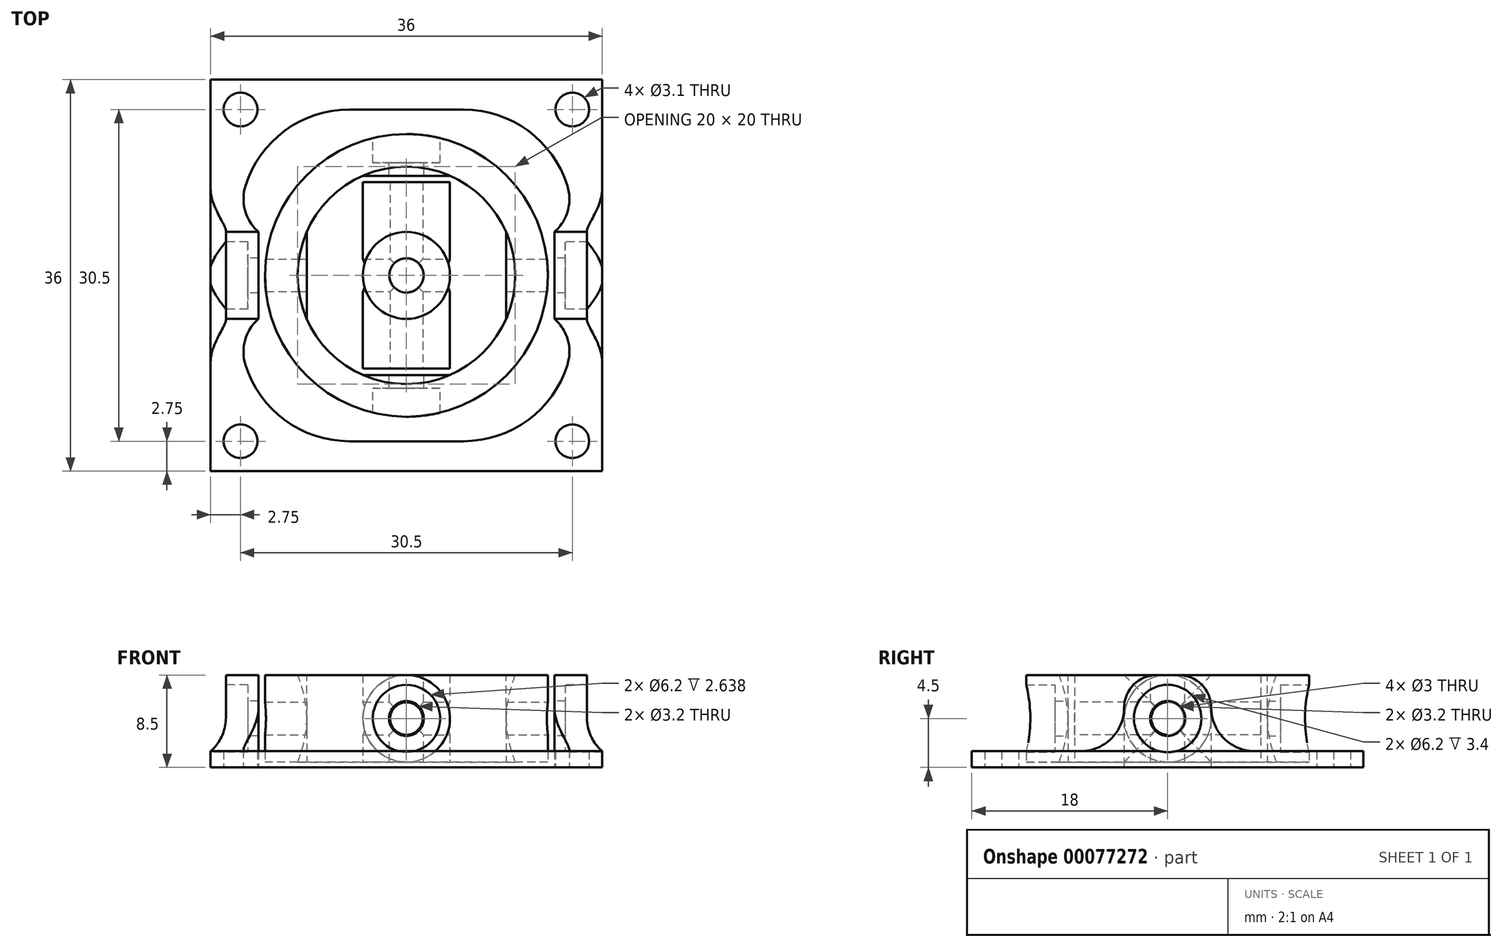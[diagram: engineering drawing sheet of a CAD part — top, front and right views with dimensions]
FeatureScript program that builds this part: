
annotation { "Feature Type Name" : "Feature", "Feature Type Description" : "" }
export const myFeature = defineFeature(function(context is Context, id is Id, definition is map)
    precondition{}
    {
        {
            var Q0;
            Q0=qCreatedBy(makeId("Top.planeOp"),FACE);
            var sketch = newSketch(context, id + "F0", { "sketchPlane" : qUnion([Q0])});
            skLineSegment(sketch, "E0.bottom", {"start": v(18, 18) * mm, "end": v(-18, 18) * mm});
            skLineSegment(sketch, "E0.top", {"start": v(18, -18) * mm, "end": v(-18, -18) * mm});
            skLineSegment(sketch, "E0.left", {"start": v(18, 18) * mm, "end": v(18, -18) * mm});
            skLineSegment(sketch, "E0.right", {"start": v(-18, 18) * mm, "end": v(-18, -18) * mm});
            skPoint(sketch, "E0.middle", {"position": v(0, 0) * mm});
            skLineSegment(sketch, "E1.bottom", {"start": v(15.25, 15.25) * mm, "end": v(-15.25, 15.25) * mm, "construction": true});
            skLineSegment(sketch, "E1.top", {"start": v(15.25, -15.25) * mm, "end": v(-15.25, -15.25) * mm, "construction": true});
            skLineSegment(sketch, "E1.left", {"start": v(15.25, 15.25) * mm, "end": v(15.25, -15.25) * mm, "construction": true});
            skLineSegment(sketch, "E1.right", {"start": v(-15.25, 15.25) * mm, "end": v(-15.25, -15.25) * mm, "construction": true});
            skCircle(sketch, "E2", {"center": v(-15.25, 15.25) * mm, "radius": 1.55 * mm, "construction": true});
            skCircle(sketch, "E3", {"center": v(15.25, 15.25) * mm, "radius": 1.55 * mm, "construction": true});
            skCircle(sketch, "E4", {"center": v(15.25, -15.25) * mm, "radius": 1.55 * mm, "construction": true});
            skCircle(sketch, "E5", {"center": v(-15.25, -15.25) * mm, "radius": 1.55 * mm, "construction": true});
            skSolve(sketch);
        }
        {
            var Q0;
            Q0=qCreatedBy(makeId("Top.planeOp"),FACE);
            var sketch = newSketch(context, id + "F1", { "sketchPlane" : qUnion([Q0])});
            skCircle(sketch, "E6", {"center": v(0, 0) * mm, "radius": 13 * mm});
            skCircle(sketch, "E7", {"center": v(0, 0) * mm, "radius": 10 * mm});
            skLineSegment(sketch, "E8", {"start": v(10, 0) * mm, "end": v(13, 0) * mm, "construction": true});
            skCircle(sketch, "E9", {"center": v(0, 0) * mm, "radius": 1.57 * mm, "construction": true});
            skCircle(sketch, "E10", {"center": v(0, 0) * mm, "radius": 4 * mm});
            skLineSegment(sketch, "E11", {"start": v(0, 4) * mm, "end": v(0, -4) * mm, "construction": true});
            skLineSegment(sketch, "E12", {"start": v(0, 0) * mm, "end": v(10, 0) * mm, "construction": true});
            skSolve(sketch);
        }
        {
            var Q0;
            Q0=qCreatedBy(makeId("Top.planeOp"),FACE);
            var sketch = newSketch(context, id + "F20", { "sketchPlane" : qUnion([Q0])});
            skCircle(sketch, "E13.0", {"center": v(0, 0) * mm, "radius": 10 * mm, "construction": true});
            skLineSegment(sketch, "E14", {"start": v(0, 9.17) * mm, "end": v(-4, 9.17) * mm});
            skLineSegment(sketch, "E15", {"start": v(0, 0) * mm, "end": v(0, -10) * mm, "construction": true});
            skLineSegment(sketch, "E16", {"start": v(-4, 9.17) * mm, "end": v(-4, 12.17) * mm});
            skLineSegment(sketch, "E17", {"start": v(-4, 12.17) * mm, "end": v(0, 12.17) * mm});
            skLineSegment(sketch, "E18", {"start": v(0, 12.17) * mm, "end": v(0, 9.17) * mm});
            skLineSegment(sketch, "E19", {"start": v(0, 0) * mm, "end": v(10, 0) * mm, "construction": true});
            skLineSegment(sketch, "E20.MirrorCS", {"start": v(-4, -12.17) * mm, "end": v(0, -12.17) * mm});
            skLineSegment(sketch, "E21.MirrorCS", {"start": v(-4, -9.17) * mm, "end": v(-4, -12.17) * mm});
            skLineSegment(sketch, "E22.MirrorCS", {"start": v(0, -12.17) * mm, "end": v(0, -9.17) * mm});
            skLineSegment(sketch, "E23.MirrorCS", {"start": v(0, -9.17) * mm, "end": v(-4, -9.17) * mm});
            skLineSegment(sketch, "E24", {"start": v(-4, 8.57) * mm, "end": v(-4, -8.57) * mm});
            skLineSegment(sketch, "E25", {"start": v(-4, 8.57) * mm, "end": v(0, 8.57) * mm});
            skLineSegment(sketch, "E26", {"start": v(-4, -8.57) * mm, "end": v(0, -8.57) * mm});
            skLineSegment(sketch, "E27", {"start": v(0, 8.57) * mm, "end": v(0, -8.57) * mm});
            skSolve(sketch);
        }
        {
            var Q0;
            Q0=qCreatedBy(makeId("Top.planeOp"),FACE);
            var sketch = newSketch(context, id + "F2", { "sketchPlane" : qUnion([Q0])});
            skLineSegment(sketch, "E28.0", {"start": v(0, -9.17) * mm, "end": v(-4, -9.17) * mm, "construction": true});
            skLineSegment(sketch, "E29.0", {"start": v(0, 9.17) * mm, "end": v(-4, 9.17) * mm, "construction": true});
            skLineSegment(sketch, "E30", {"start": v(0, 9.17) * mm, "end": v(0, 10.37) * mm, "construction": true});
            skLineSegment(sketch, "E31", {"start": v(0, 0) * mm, "end": v(0, 9.17) * mm, "construction": true});
            skLineSegment(sketch, "E32.bottom", {"start": v(0, 10.37) * mm, "end": v(-3.1, 10.37) * mm});
            skLineSegment(sketch, "E32.top", {"start": v(0, 16.03) * mm, "end": v(-3.1, 16.03) * mm});
            skLineSegment(sketch, "E32.left", {"start": v(0, 10.37) * mm, "end": v(0, 16.03) * mm});
            skLineSegment(sketch, "E32.right", {"start": v(-3.1, 10.37) * mm, "end": v(-3.1, 16.03) * mm});
            skLineSegment(sketch, "E33.bottom", {"start": v(0, 9.17) * mm, "end": v(-1.6, 9.17) * mm});
            skLineSegment(sketch, "E33.top", {"start": v(0, 10.37) * mm, "end": v(-1.6, 10.37) * mm});
            skLineSegment(sketch, "E33.left", {"start": v(0, 9.17) * mm, "end": v(0, 10.37) * mm});
            skLineSegment(sketch, "E33.right", {"start": v(-1.6, 9.17) * mm, "end": v(-1.6, 10.37) * mm});
            skLineSegment(sketch, "E34", {"start": v(0, 0) * mm, "end": v(12.38, 0) * mm, "construction": true});
            skLineSegment(sketch, "E35.MirrorCS", {"start": v(-3.1, -10.37) * mm, "end": v(-3.1, -16.03) * mm});
            skLineSegment(sketch, "E36.MirrorCS", {"start": v(0, -10.37) * mm, "end": v(0, -16.03) * mm});
            skLineSegment(sketch, "E37.MirrorCS", {"start": v(0, -10.37) * mm, "end": v(-3.1, -10.37) * mm});
            skLineSegment(sketch, "E38.MirrorCS", {"start": v(0, -9.17) * mm, "end": v(0, -10.37) * mm, "construction": true});
            skLineSegment(sketch, "E39.MirrorCS", {"start": v(0, -16.03) * mm, "end": v(-3.1, -16.03) * mm});
            skLineSegment(sketch, "E40.MirrorCS", {"start": v(-1.6, -9.17) * mm, "end": v(-1.6, -10.37) * mm});
            skLineSegment(sketch, "E41", {"start": v(-1.6, -9.17) * mm, "end": v(0, -9.17) * mm});
            skLineSegment(sketch, "E42", {"start": v(0, -10.37) * mm, "end": v(0, -9.17) * mm});
            skSolve(sketch);
        }
        {
            var Q0;
            Q0=makeQuery(id+"F1.imprint","IMPRINT",FACE,{"disambiguationData":[TD([[makeQuery(id+"F1.imprint","IMPRINT",EDGE,{"derivedFrom":sQuery(id+"F1.wireOp",EDGE,"E10")}),1.0]])]});
            extrude(context, id + "F3", {"entities" : qUnion([Q0]), "endBound" : BoundingType.SYMMETRIC, "depth" : 8 * mm});
        }
        {
            var Q0;
            Q0=makeQuery(id+"F1.imprint","IMPRINT",FACE,{"disambiguationData":[TD([[makeQuery(id+"F1.imprint","IMPRINT",EDGE,{"derivedFrom":sQuery(id+"F1.wireOp",EDGE,"E6")}),1.0]])]});
            extrude(context, id + "F4", {"entities" : qUnion([Q0]), "endBound" : BoundingType.SYMMETRIC, "depth" : 8 * mm});
        }
        {
            var Q0;
            Q0=makeQuery(id+"F20.imprint","IMPRINT",FACE,{"disambiguationData":[TD([[makeQuery(id+"F20.imprint","IMPRINT",EDGE,{"derivedFrom":sQuery(id+"F20.wireOp",EDGE,"E14")}),-1.0]])]});
            var Q1;
            Q1=sQuery(id+"F20.wireOp",EDGE,"E15");
            revolve(context, id + "F5", {"entities" : qUnion([Q0]), "axis" : qUnion([Q1]), "revolveType" : RevolveType.FULL});
        }
        {
            var Q0;
            Q0=makeQuery(id+"F20.imprint","IMPRINT",FACE,{"disambiguationData":[TD([[makeQuery(id+"F20.imprint","IMPRINT",EDGE,{"derivedFrom":sQuery(id+"F20.wireOp",EDGE,"E24")}),1.0]])]});
            var Q1;
            Q1=sQuery(id+"F20.wireOp",EDGE,"E27");
            revolve(context, id + "F21", {"operationType" : NewBodyOperationType.ADD, "entities" : qUnion([Q0]), "axis" : qUnion([Q1]), "revolveType" : RevolveType.FULL});
        }
        {
            var Q0;
            Q0=qCreatedBy(makeId("Front.planeOp"),FACE);
            var sketch = newSketch(context, id + "F22", { "sketchPlane" : qUnion([Q0])});
            skLineSegment(sketch, "E43", {"start": v(0, 0) * mm, "end": v(0, 28.15) * mm, "construction": true});
            skSolve(sketch);
        }
        {
            var Q0;
            Q0=makeQuery(id+"F5.opRevolve","SWEPT_BODY",BODY,{"disambiguationData":[OSD([sQuery(id+"F20.wireOp",EDGE,"E14"),sQuery(id+"F20.wireOp",EDGE,"E16"),sQuery(id+"F20.wireOp",EDGE,"E17"),sQuery(id+"F20.wireOp",EDGE,"E18")])]});
            var Q1;
            Q1=sQuery(id+"F22.wireOp",EDGE,"E43");
            circularPattern(context, id + "F6", {"operationType" : NewBodyOperationType.ADD, "entities" : qUnion([Q0]), "axis" : qUnion([Q1]), "angle" : 90 * degree, "instanceCount" : 4});
        }
        {
            var Q0;
            Q0=makeQuery(id+"F2.imprint","IMPRINT",FACE,{"disambiguationData":[TD([[makeQuery(id+"F2.imprint","IMPRINT",EDGE,{"derivedFrom":sQuery(id+"F2.wireOp",EDGE,"E32.bottom")}),-1.0]])]});
            var Q1;
            {var subQ1=sQuery(id+"F2.wireOp",EDGE,"E35.MirrorCS");Q1=makeQuery(id+"F2.imprint","IMPRINT",FACE,{"disambiguationData":[TD([[makeQuery(id+"F2.imprint","IMPRINT",EDGE,{"derivedFrom":subQ1}),1.0]])]});}
            var Q2;
            {var subQ2=sQuery(id+"F2.wireOp",EDGE,"E40.MirrorCS");Q2=makeQuery(id+"F2.imprint","IMPRINT",FACE,{"disambiguationData":[TD([[makeQuery(id+"F2.imprint","IMPRINT",EDGE,{"derivedFrom":subQ2}),1.0]])]});}
            var Q3;
            Q3=makeQuery(id+"F2.imprint","IMPRINT",FACE,{"disambiguationData":[TD([[makeQuery(id+"F2.imprint","IMPRINT",EDGE,{"derivedFrom":sQuery(id+"F2.wireOp",EDGE,"E33.bottom")}),-1.0]])]});
            var Q4;
            Q4=sQuery(id+"F2.wireOp",EDGE,"E31");
            revolve(context, id + "F23", {"operationType" : NewBodyOperationType.REMOVE, "entities" : qUnion([Q0, Q1, Q2, Q3]), "axis" : qUnion([Q4]), "revolveType" : RevolveType.FULL, "oppositeDirection" : true});
        }
        {
            var Q0;
            Q0=qCreatedBy(makeId("Top.planeOp"),FACE);
            var sketch = newSketch(context, id + "F24", { "sketchPlane" : qUnion([Q0])});
            skCircle(sketch, "E44.0", {"center": v(0, 0) * mm, "radius": 1.57 * mm});
            skSolve(sketch);
        }
        {
            var Q0;
            Q0=makeQuery(id+"F24.imprint","IMPRINT",FACE,{"disambiguationData":[TD([[makeQuery(id+"F24.imprint","IMPRINT",EDGE,{"derivedFrom":sQuery(id+"F24.wireOp",EDGE,"E44.0")}),1.0]])]});
            extrude(context, id + "F7", {"entities" : qUnion([Q0]), "operationType" : NewBodyOperationType.REMOVE, "endBound" : BoundingType.THROUGH_ALL, "oppositeDirection" : true, "depth" : 25 * mm, "hasSecondDirection" : true, "secondDirectionBound" : SecondDirectionBoundingType.THROUGH_ALL, "secondDirectionOppositeDirection" : false, "secondDirectionDepth" : 25 * mm});
        }
        {
            var Q0;
            Q0=qCreatedBy(makeId("Front.planeOp"),FACE);
            var sketch = newSketch(context, id + "F8", { "sketchPlane" : qUnion([Q0])});
            skCircle(sketch, "E45", {"center": v(0, 0) * mm, "radius": 1.5 * mm});
            skSolve(sketch);
        }
        {
            var Q0;
            Q0=makeQuery(id+"F8.imprint","IMPRINT",FACE,{"disambiguationData":[TD([[makeQuery(id+"F8.imprint","IMPRINT",EDGE,{"derivedFrom":sQuery(id+"F8.wireOp",EDGE,"E45")}),1.0]])]});
            extrude(context, id + "F25", {"entities" : qUnion([Q0]), "operationType" : NewBodyOperationType.REMOVE, "endBound" : BoundingType.THROUGH_ALL, "oppositeDirection" : true, "depth" : 25 * mm, "hasSecondDirection" : true, "secondDirectionOppositeDirection" : false, "secondDirectionDepth" : 25 * mm});
        }
        {
            var Q0;
            Q0=qCreatedBy(makeId("Right.planeOp"),FACE);
            var sketch = newSketch(context, id + "F9", { "sketchPlane" : qUnion([Q0])});
            skCircle(sketch, "E46", {"center": v(0, 0) * mm, "radius": 1.5 * mm});
            skSolve(sketch);
        }
        {
            var Q0;
            Q0=makeQuery(id+"F9.imprint","IMPRINT",FACE,{"disambiguationData":[TD([[makeQuery(id+"F9.imprint","IMPRINT",EDGE,{"derivedFrom":sQuery(id+"F9.wireOp",EDGE,"E46")}),1.0]])]});
            extrude(context, id + "F26", {"entities" : qUnion([Q0]), "operationType" : NewBodyOperationType.REMOVE, "endBound" : BoundingType.THROUGH_ALL, "oppositeDirection" : true, "depth" : 25 * mm, "hasSecondDirection" : true, "secondDirectionBound" : SecondDirectionBoundingType.THROUGH_ALL, "secondDirectionOppositeDirection" : false, "secondDirectionDepth" : 25 * mm});
        }
        {
            var Q0;
            Q0=qCreatedBy(makeId("Top.planeOp"),FACE);
            var sketch = newSketch(context, id + "F10", { "sketchPlane" : qUnion([Q0])});
            skLineSegment(sketch, "E47.0", {"start": v(-18, 18) * mm, "end": v(-18, -18) * mm});
            skLineSegment(sketch, "E48.0", {"start": v(18, 18) * mm, "end": v(-18, 18) * mm});
            skLineSegment(sketch, "E49.0", {"start": v(18, 18) * mm, "end": v(18, -18) * mm});
            skLineSegment(sketch, "E50.0", {"start": v(18, -18) * mm, "end": v(-18, -18) * mm});
            skCircle(sketch, "E51.0", {"center": v(-15.25, 15.25) * mm, "radius": 1.55 * mm});
            skCircle(sketch, "E52.0", {"center": v(15.25, 15.25) * mm, "radius": 1.55 * mm});
            skCircle(sketch, "E53.0", {"center": v(-15.25, -15.25) * mm, "radius": 1.55 * mm});
            skCircle(sketch, "E54.0", {"center": v(15.25, -15.25) * mm, "radius": 1.55 * mm});
            skLineSegment(sketch, "E55", {"start": v(-5.25, 15.25) * mm, "end": v(5.25, 15.25) * mm});
            skLineSegment(sketch, "E56", {"start": v(15.25, -5.25) * mm, "end": v(15.25, -4) * mm});
            skLineSegment(sketch, "E57", {"start": v(-5.25, -15.25) * mm, "end": v(5.25, -15.25) * mm});
            skLineSegment(sketch, "E58", {"start": v(-15.25, 5.25) * mm, "end": v(-15.25, 4) * mm});
            skArc(sketch, "E59.filletArc", {"start": v(-5.25, 15.25) * mm, "mid": v(-12.32, 12.32) * mm, "end": v(-15.25, 5.25) * mm});
            skArc(sketch, "E60.filletArc", {"start": v(15.25, 5.25) * mm, "mid": v(12.32, 12.32) * mm, "end": v(5.25, 15.25) * mm});
            skArc(sketch, "E61.filletArc", {"start": v(-15.25, -5.25) * mm, "mid": v(-12.32, -12.32) * mm, "end": v(-5.25, -15.25) * mm});
            skArc(sketch, "E62.filletArc", {"start": v(5.25, -15.25) * mm, "mid": v(12.32, -12.32) * mm, "end": v(15.25, -5.25) * mm});
            skCircle(sketch, "E63.0", {"center": v(0, 0) * mm, "radius": 13 * mm, "construction": true});
            skLineSegment(sketch, "E64", {"start": v(-13, 0) * mm, "end": v(-13.6, 0) * mm, "construction": true});
            skLineSegment(sketch, "E65", {"start": v(-13.6, 4) * mm, "end": v(-13.6, -4) * mm});
            skLineSegment(sketch, "E66", {"start": v(-13.6, 4) * mm, "end": v(-15.25, 4) * mm});
            skLineSegment(sketch, "E67", {"start": v(-13.6, -4) * mm, "end": v(-15.25, -4) * mm});
            skLineSegment(sketch, "E68.MirrorCS", {"start": v(13.6, 4) * mm, "end": v(15.25, 4) * mm});
            skLineSegment(sketch, "E69.MirrorCS", {"start": v(13.6, 4) * mm, "end": v(13.6, -4) * mm});
            skLineSegment(sketch, "E70.MirrorCS", {"start": v(13.6, -4) * mm, "end": v(15.25, -4) * mm});
            skLineSegment(sketch, "E71.trimOffspring", {"start": v(-15.25, -4) * mm, "end": v(-15.25, -5.25) * mm});
            skLineSegment(sketch, "E72.trimOffspring", {"start": v(15.25, 4) * mm, "end": v(15.25, 5.25) * mm});
            skSolve(sketch);
        }
        {
            var Q0;
            Q0=makeQuery(id+"F10.imprint","IMPRINT",FACE,{"disambiguationData":[TD([[makeQuery(id+"F10.imprint","IMPRINT",EDGE,{"derivedFrom":sQuery(id+"F10.wireOp",EDGE,"E47.0")}),1.0]])]});
            extrude(context, id + "F11", {"entities" : qUnion([Q0]), "depth" : 1.5 * mm});
        }
        {
            var Q0;
            Q0=qCreatedBy(makeId("Top.planeOp"),FACE);
            var sketch = newSketch(context, id + "F12", { "sketchPlane" : qUnion([Q0])});
            skLineSegment(sketch, "E73.0", {"start": v(-13.6, 4) * mm, "end": v(-13.6, -4) * mm});
            skLineSegment(sketch, "E74", {"start": v(-13.6, 4) * mm, "end": v(-16.6, 4) * mm});
            skLineSegment(sketch, "E75", {"start": v(-13.6, -4) * mm, "end": v(-16.6, -4) * mm});
            skLineSegment(sketch, "E76", {"start": v(-16.6, -4) * mm, "end": v(-16.6, 4) * mm});
            skLineSegment(sketch, "E77.MirrorCS", {"start": v(13.6, 4) * mm, "end": v(16.6, 4) * mm});
            skLineSegment(sketch, "E78.MirrorCS", {"start": v(16.6, -4) * mm, "end": v(16.6, 4) * mm});
            skLineSegment(sketch, "E79.MirrorCS", {"start": v(13.6, -4) * mm, "end": v(16.6, -4) * mm});
            skLineSegment(sketch, "E80.MirrorCS", {"start": v(13.6, 4) * mm, "end": v(13.6, -4) * mm});
            skPoint(sketch, "E81", {"position": v(-16.6, 0) * mm});
            skLineSegment(sketch, "E82", {"start": v(-14.6, -3.1) * mm, "end": v(-18, -3.1) * mm});
            skLineSegment(sketch, "E83", {"start": v(-14.6, -3.1) * mm, "end": v(-14.6, -1.6) * mm});
            skLineSegment(sketch, "E84", {"start": v(-14.6, -1.6) * mm, "end": v(-13.6, -1.6) * mm});
            skLineSegment(sketch, "E85", {"start": v(-16.6, 0) * mm, "end": v(-13.6, 0) * mm});
            skLineSegment(sketch, "E86.MirrorCS", {"start": v(14.6, -1.6) * mm, "end": v(13.6, -1.6) * mm});
            skLineSegment(sketch, "E87.MirrorCS", {"start": v(14.6, -3.1) * mm, "end": v(14.6, -1.6) * mm});
            skLineSegment(sketch, "E88.MirrorCS", {"start": v(14.6, -3.1) * mm, "end": v(18, -3.1) * mm});
            skLineSegment(sketch, "E89.MirrorCS", {"start": v(16.6, 0) * mm, "end": v(13.6, 0) * mm});
            skLineSegment(sketch, "E90", {"start": v(-18, -3.1) * mm, "end": v(-18, 0) * mm});
            skLineSegment(sketch, "E91", {"start": v(-18, 0) * mm, "end": v(-16.6, 0) * mm});
            skLineSegment(sketch, "E92.MirrorCS", {"start": v(18, 0) * mm, "end": v(16.6, 0) * mm});
            skLineSegment(sketch, "E93.MirrorCS", {"start": v(18, -3.1) * mm, "end": v(18, 0) * mm});
            skSolve(sketch);
        }
        {
            var Q0;
            {var subQ0=sQuery(id+"F12.wireOp",EDGE,"E74");Q0=makeQuery(id+"F12.imprint","IMPRINT",FACE,{"disambiguationData":[TD([[makeQuery(id+"F12.imprint","IMPRINT",EDGE,{"derivedFrom":subQ0}),1.0]])]});}
            var Q1;
            {var subQ0=sQuery(id+"F12.wireOp",EDGE,"E83");Q1=makeQuery(id+"F12.imprint","IMPRINT",FACE,{"disambiguationData":[TD([[makeQuery(id+"F12.imprint","IMPRINT",EDGE,{"derivedFrom":subQ0}),1.0]])]});}
            var Q2;
            {var subQ4=sQuery(id+"F12.wireOp",EDGE,"E75");Q2=makeQuery(id+"F12.imprint","IMPRINT",FACE,{"disambiguationData":[TD([[makeQuery(id+"F12.imprint","IMPRINT",EDGE,{"derivedFrom":subQ4}),-1.0]])]});}
            var Q3;
            {var subQ0=sQuery(id+"F12.wireOp",EDGE,"E77.MirrorCS");Q3=makeQuery(id+"F12.imprint","IMPRINT",FACE,{"disambiguationData":[TD([[makeQuery(id+"F12.imprint","IMPRINT",EDGE,{"derivedFrom":subQ0}),-1.0]])]});}
            var Q4;
            {var subQ0=sQuery(id+"F12.wireOp",EDGE,"E86.MirrorCS");Q4=makeQuery(id+"F12.imprint","IMPRINT",FACE,{"disambiguationData":[TD([[makeQuery(id+"F12.imprint","IMPRINT",EDGE,{"derivedFrom":subQ0}),-1.0]])]});}
            var Q5;
            {var subQ1=sQuery(id+"F12.wireOp",EDGE,"E79.MirrorCS");Q5=makeQuery(id+"F12.imprint","IMPRINT",FACE,{"disambiguationData":[TD([[makeQuery(id+"F12.imprint","IMPRINT",EDGE,{"derivedFrom":subQ1}),1.0]])]});}
            extrude(context, id + "F13", {"entities" : qUnion([Q0, Q1, Q2, Q3, Q4, Q5]), "operationType" : NewBodyOperationType.ADD, "depth" : 8.5 * mm});
        }
        {
            var Q0;
            {var subQ0=sQuery(id+"F12.wireOp",EDGE,"E83");Q0=makeQuery(id+"F12.imprint","IMPRINT",FACE,{"disambiguationData":[TD([[makeQuery(id+"F12.imprint","IMPRINT",EDGE,{"derivedFrom":subQ0}),1.0]])]});}
            var Q1;
            {var subQ4=sQuery(id+"F12.wireOp",EDGE,"E90");Q1=makeQuery(id+"F12.imprint","IMPRINT",FACE,{"disambiguationData":[TD([[makeQuery(id+"F12.imprint","IMPRINT",EDGE,{"derivedFrom":subQ4}),-1.0]])]});}
            var Q2;
            {var subQ0=sQuery(id+"F12.wireOp",EDGE,"E92.MirrorCS");Q2=makeQuery(id+"F12.imprint","IMPRINT",FACE,{"disambiguationData":[TD([[makeQuery(id+"F12.imprint","IMPRINT",EDGE,{"derivedFrom":subQ0}),1.0]])]});}
            var Q3;
            {var subQ0=sQuery(id+"F12.wireOp",EDGE,"E86.MirrorCS");Q3=makeQuery(id+"F12.imprint","IMPRINT",FACE,{"disambiguationData":[TD([[makeQuery(id+"F12.imprint","IMPRINT",EDGE,{"derivedFrom":subQ0}),-1.0]])]});}
            var Q4;
            Q4=sQuery(id+"F12.wireOp",EDGE,"E85");
            revolve(context, id + "F14", {"entities" : qUnion([Q0, Q1, Q2, Q3]), "axis" : qUnion([Q4]), "revolveType" : RevolveType.FULL});
        }
        {
            var Q0;
            Q0=makeQuery(id+"F11.opExtrude","SWEPT_BODY",BODY,{"disambiguationData":[OSD([sQuery(id+"F10.wireOp",EDGE,"E47.0"),sQuery(id+"F10.wireOp",EDGE,"E48.0"),sQuery(id+"F10.wireOp",EDGE,"E49.0"),sQuery(id+"F10.wireOp",EDGE,"E50.0"),sQuery(id+"F10.wireOp",EDGE,"E51.0"),sQuery(id+"F10.wireOp",EDGE,"E52.0"),sQuery(id+"F10.wireOp",EDGE,"E53.0"),sQuery(id+"F10.wireOp",EDGE,"E54.0"),sQuery(id+"F10.wireOp",EDGE,"E55"),sQuery(id+"F10.wireOp",EDGE,"E56"),sQuery(id+"F10.wireOp",EDGE,"E57"),sQuery(id+"F10.wireOp",EDGE,"E58"),sQuery(id+"F10.wireOp",EDGE,"E59.filletArc"),sQuery(id+"F10.wireOp",EDGE,"E60.filletArc"),sQuery(id+"F10.wireOp",EDGE,"E61.filletArc"),sQuery(id+"F10.wireOp",EDGE,"E62.filletArc"),sQuery(id+"F10.wireOp",EDGE,"E65"),sQuery(id+"F10.wireOp",EDGE,"E66"),sQuery(id+"F10.wireOp",EDGE,"E67"),sQuery(id+"F10.wireOp",EDGE,"E68.MirrorCS"),sQuery(id+"F10.wireOp",EDGE,"E69.MirrorCS"),sQuery(id+"F10.wireOp",EDGE,"E70.MirrorCS"),sQuery(id+"F10.wireOp",EDGE,"E71.trimOffspring"),sQuery(id+"F10.wireOp",EDGE,"E72.trimOffspring")])]});
            transform(context, id + "F15", {"entities" : qUnion([Q0]), "transformType" : TransformType.TRANSLATION_3D, "dx" : 0 * mm, "dy" : 0 * mm, "dz" : (-1.5 - 3) * mm, "makeCopy" : false});
        }
        {
            var Q0;
            Q0=makeQuery(id+"F14.opRevolve","SWEPT_BODY",BODY,{"disambiguationData":[OSD([sQuery(id+"F12.wireOp",EDGE,"E73.0"),sQuery(id+"F12.wireOp",EDGE,"E82"),sQuery(id+"F12.wireOp",EDGE,"E83"),sQuery(id+"F12.wireOp",EDGE,"E84"),sQuery(id+"F12.wireOp",EDGE,"E85"),sQuery(id+"F12.wireOp",EDGE,"E90"),sQuery(id+"F12.wireOp",EDGE,"E91")])]});
            var Q1;
            Q1=makeQuery(id+"F14.opRevolve","SWEPT_BODY",BODY,{"disambiguationData":[OSD([sQuery(id+"F12.wireOp",EDGE,"E80.MirrorCS"),sQuery(id+"F12.wireOp",EDGE,"E86.MirrorCS"),sQuery(id+"F12.wireOp",EDGE,"E87.MirrorCS"),sQuery(id+"F12.wireOp",EDGE,"E88.MirrorCS"),sQuery(id+"F12.wireOp",EDGE,"E89.MirrorCS"),sQuery(id+"F12.wireOp",EDGE,"E92.MirrorCS"),sQuery(id+"F12.wireOp",EDGE,"E93.MirrorCS")])]});
            var Q2;
            Q2=makeQuery(id+"F11.opExtrude","SWEPT_BODY",BODY,{"disambiguationData":[OSD([sQuery(id+"F10.wireOp",EDGE,"E47.0"),sQuery(id+"F10.wireOp",EDGE,"E48.0"),sQuery(id+"F10.wireOp",EDGE,"E49.0"),sQuery(id+"F10.wireOp",EDGE,"E50.0"),sQuery(id+"F10.wireOp",EDGE,"E51.0"),sQuery(id+"F10.wireOp",EDGE,"E52.0"),sQuery(id+"F10.wireOp",EDGE,"E53.0"),sQuery(id+"F10.wireOp",EDGE,"E54.0"),sQuery(id+"F10.wireOp",EDGE,"E55"),sQuery(id+"F10.wireOp",EDGE,"E56"),sQuery(id+"F10.wireOp",EDGE,"E57"),sQuery(id+"F10.wireOp",EDGE,"E58"),sQuery(id+"F10.wireOp",EDGE,"E59.filletArc"),sQuery(id+"F10.wireOp",EDGE,"E60.filletArc"),sQuery(id+"F10.wireOp",EDGE,"E61.filletArc"),sQuery(id+"F10.wireOp",EDGE,"E62.filletArc"),sQuery(id+"F10.wireOp",EDGE,"E65"),sQuery(id+"F10.wireOp",EDGE,"E66"),sQuery(id+"F10.wireOp",EDGE,"E67"),sQuery(id+"F10.wireOp",EDGE,"E68.MirrorCS"),sQuery(id+"F10.wireOp",EDGE,"E69.MirrorCS"),sQuery(id+"F10.wireOp",EDGE,"E70.MirrorCS"),sQuery(id+"F10.wireOp",EDGE,"E71.trimOffspring"),sQuery(id+"F10.wireOp",EDGE,"E72.trimOffspring")])]});
            booleanBodies(context, id + "F16", {"operationType" : BooleanOperationType.SUBTRACTION, "tools" : qUnion([Q0, Q1]), "targets" : qUnion([Q2])});
        }
        {
            var Q0;
            {var subQ0=makeQuery(id+"F13.opExtrude","SWEPT_FACE",FACE,{"disambiguationData":[OSD([sQuery(id+"F12.wireOp",EDGE,"E76")])]});var subQ1=sQuery(id+"F10.wireOp",EDGE,"E66");var subQ2=makeQuery(id+"F11.opExtrude","CAP_FACE",FACE,{"disambiguationData":[OSD([sQuery(id+"F10.wireOp",EDGE,"E47.0"),sQuery(id+"F10.wireOp",EDGE,"E48.0"),sQuery(id+"F10.wireOp",EDGE,"E49.0"),sQuery(id+"F10.wireOp",EDGE,"E50.0"),sQuery(id+"F10.wireOp",EDGE,"E51.0"),sQuery(id+"F10.wireOp",EDGE,"E52.0"),sQuery(id+"F10.wireOp",EDGE,"E53.0"),sQuery(id+"F10.wireOp",EDGE,"E54.0"),sQuery(id+"F10.wireOp",EDGE,"E55"),sQuery(id+"F10.wireOp",EDGE,"E56"),sQuery(id+"F10.wireOp",EDGE,"E57"),sQuery(id+"F10.wireOp",EDGE,"E58"),sQuery(id+"F10.wireOp",EDGE,"E59.filletArc"),sQuery(id+"F10.wireOp",EDGE,"E60.filletArc"),sQuery(id+"F10.wireOp",EDGE,"E61.filletArc"),sQuery(id+"F10.wireOp",EDGE,"E62.filletArc"),sQuery(id+"F10.wireOp",EDGE,"E65"),subQ1,sQuery(id+"F10.wireOp",EDGE,"E67"),sQuery(id+"F10.wireOp",EDGE,"E68.MirrorCS"),sQuery(id+"F10.wireOp",EDGE,"E69.MirrorCS"),sQuery(id+"F10.wireOp",EDGE,"E70.MirrorCS"),sQuery(id+"F10.wireOp",EDGE,"E71.trimOffspring"),sQuery(id+"F10.wireOp",EDGE,"E72.trimOffspring")])],"isStart":false});Q0=makeQuery(id+"F16.opBoolean","SPLIT",EDGE,{"disambiguationData":[TD([makeQuery(id+"F11.opExtrude","SWEPT_FACE",FACE,{"disambiguationData":[OSD([subQ1])]})])],"derivedFrom":makeQuery(id+"F13.boolean.opBoolean","INTERSECT",EDGE,{"derivedFrom":[subQ2,subQ0]})});}
            var Q1;
            {var subQ0=makeQuery(id+"F13.opExtrude","SWEPT_FACE",FACE,{"disambiguationData":[OSD([sQuery(id+"F12.wireOp",EDGE,"E76")])]});var subQ1=sQuery(id+"F10.wireOp",EDGE,"E67");var subQ2=makeQuery(id+"F11.opExtrude","CAP_FACE",FACE,{"disambiguationData":[OSD([sQuery(id+"F10.wireOp",EDGE,"E47.0"),sQuery(id+"F10.wireOp",EDGE,"E48.0"),sQuery(id+"F10.wireOp",EDGE,"E49.0"),sQuery(id+"F10.wireOp",EDGE,"E50.0"),sQuery(id+"F10.wireOp",EDGE,"E51.0"),sQuery(id+"F10.wireOp",EDGE,"E52.0"),sQuery(id+"F10.wireOp",EDGE,"E53.0"),sQuery(id+"F10.wireOp",EDGE,"E54.0"),sQuery(id+"F10.wireOp",EDGE,"E55"),sQuery(id+"F10.wireOp",EDGE,"E56"),sQuery(id+"F10.wireOp",EDGE,"E57"),sQuery(id+"F10.wireOp",EDGE,"E58"),sQuery(id+"F10.wireOp",EDGE,"E59.filletArc"),sQuery(id+"F10.wireOp",EDGE,"E60.filletArc"),sQuery(id+"F10.wireOp",EDGE,"E61.filletArc"),sQuery(id+"F10.wireOp",EDGE,"E62.filletArc"),sQuery(id+"F10.wireOp",EDGE,"E65"),sQuery(id+"F10.wireOp",EDGE,"E66"),subQ1,sQuery(id+"F10.wireOp",EDGE,"E68.MirrorCS"),sQuery(id+"F10.wireOp",EDGE,"E69.MirrorCS"),sQuery(id+"F10.wireOp",EDGE,"E70.MirrorCS"),sQuery(id+"F10.wireOp",EDGE,"E71.trimOffspring"),sQuery(id+"F10.wireOp",EDGE,"E72.trimOffspring")])],"isStart":false});Q1=makeQuery(id+"F16.opBoolean","SPLIT",EDGE,{"disambiguationData":[TD([makeQuery(id+"F11.opExtrude","SWEPT_FACE",FACE,{"disambiguationData":[OSD([subQ1])]})])],"derivedFrom":makeQuery(id+"F13.boolean.opBoolean","INTERSECT",EDGE,{"derivedFrom":[subQ2,subQ0]})});}
            var Q2;
            {var subQ0=makeQuery(id+"F13.opExtrude","SWEPT_FACE",FACE,{"disambiguationData":[OSD([sQuery(id+"F12.wireOp",EDGE,"E78.MirrorCS")])]});var subQ1=sQuery(id+"F10.wireOp",EDGE,"E70.MirrorCS");var subQ2=makeQuery(id+"F11.opExtrude","CAP_FACE",FACE,{"disambiguationData":[OSD([sQuery(id+"F10.wireOp",EDGE,"E47.0"),sQuery(id+"F10.wireOp",EDGE,"E48.0"),sQuery(id+"F10.wireOp",EDGE,"E49.0"),sQuery(id+"F10.wireOp",EDGE,"E50.0"),sQuery(id+"F10.wireOp",EDGE,"E51.0"),sQuery(id+"F10.wireOp",EDGE,"E52.0"),sQuery(id+"F10.wireOp",EDGE,"E53.0"),sQuery(id+"F10.wireOp",EDGE,"E54.0"),sQuery(id+"F10.wireOp",EDGE,"E55"),sQuery(id+"F10.wireOp",EDGE,"E56"),sQuery(id+"F10.wireOp",EDGE,"E57"),sQuery(id+"F10.wireOp",EDGE,"E58"),sQuery(id+"F10.wireOp",EDGE,"E59.filletArc"),sQuery(id+"F10.wireOp",EDGE,"E60.filletArc"),sQuery(id+"F10.wireOp",EDGE,"E61.filletArc"),sQuery(id+"F10.wireOp",EDGE,"E62.filletArc"),sQuery(id+"F10.wireOp",EDGE,"E65"),sQuery(id+"F10.wireOp",EDGE,"E66"),sQuery(id+"F10.wireOp",EDGE,"E67"),sQuery(id+"F10.wireOp",EDGE,"E68.MirrorCS"),sQuery(id+"F10.wireOp",EDGE,"E69.MirrorCS"),subQ1,sQuery(id+"F10.wireOp",EDGE,"E71.trimOffspring"),sQuery(id+"F10.wireOp",EDGE,"E72.trimOffspring")])],"isStart":false});Q2=makeQuery(id+"F16.opBoolean","SPLIT",EDGE,{"disambiguationData":[TD([makeQuery(id+"F11.opExtrude","SWEPT_FACE",FACE,{"disambiguationData":[OSD([subQ1])]})])],"derivedFrom":makeQuery(id+"F13.boolean.opBoolean","INTERSECT",EDGE,{"derivedFrom":[subQ2,subQ0]})});}
            var Q3;
            {var subQ0=makeQuery(id+"F13.opExtrude","SWEPT_FACE",FACE,{"disambiguationData":[OSD([sQuery(id+"F12.wireOp",EDGE,"E78.MirrorCS")])]});var subQ1=sQuery(id+"F10.wireOp",EDGE,"E68.MirrorCS");var subQ2=makeQuery(id+"F11.opExtrude","CAP_FACE",FACE,{"disambiguationData":[OSD([sQuery(id+"F10.wireOp",EDGE,"E47.0"),sQuery(id+"F10.wireOp",EDGE,"E48.0"),sQuery(id+"F10.wireOp",EDGE,"E49.0"),sQuery(id+"F10.wireOp",EDGE,"E50.0"),sQuery(id+"F10.wireOp",EDGE,"E51.0"),sQuery(id+"F10.wireOp",EDGE,"E52.0"),sQuery(id+"F10.wireOp",EDGE,"E53.0"),sQuery(id+"F10.wireOp",EDGE,"E54.0"),sQuery(id+"F10.wireOp",EDGE,"E55"),sQuery(id+"F10.wireOp",EDGE,"E56"),sQuery(id+"F10.wireOp",EDGE,"E57"),sQuery(id+"F10.wireOp",EDGE,"E58"),sQuery(id+"F10.wireOp",EDGE,"E59.filletArc"),sQuery(id+"F10.wireOp",EDGE,"E60.filletArc"),sQuery(id+"F10.wireOp",EDGE,"E61.filletArc"),sQuery(id+"F10.wireOp",EDGE,"E62.filletArc"),sQuery(id+"F10.wireOp",EDGE,"E65"),sQuery(id+"F10.wireOp",EDGE,"E66"),sQuery(id+"F10.wireOp",EDGE,"E67"),subQ1,sQuery(id+"F10.wireOp",EDGE,"E69.MirrorCS"),sQuery(id+"F10.wireOp",EDGE,"E70.MirrorCS"),sQuery(id+"F10.wireOp",EDGE,"E71.trimOffspring"),sQuery(id+"F10.wireOp",EDGE,"E72.trimOffspring")])],"isStart":false});Q3=makeQuery(id+"F16.opBoolean","SPLIT",EDGE,{"disambiguationData":[TD([makeQuery(id+"F11.opExtrude","SWEPT_FACE",FACE,{"disambiguationData":[OSD([subQ1])]})])],"derivedFrom":makeQuery(id+"F13.boolean.opBoolean","INTERSECT",EDGE,{"derivedFrom":[subQ2,subQ0]})});}
            var Q4;
            Q4=makeQuery(id+"F11.opExtrude","SWEPT_EDGE",EDGE,{"disambiguationData":[OSD([sQuery(id+"F10.wireOp",EDGE,"E56"),sQuery(id+"F10.wireOp",EDGE,"E70.MirrorCS")])]});
            var Q5;
            Q5=makeQuery(id+"F11.opExtrude","SWEPT_EDGE",EDGE,{"disambiguationData":[OSD([sQuery(id+"F10.wireOp",EDGE,"E68.MirrorCS"),sQuery(id+"F10.wireOp",EDGE,"E72.trimOffspring")])]});
            var Q6;
            Q6=makeQuery(id+"F11.opExtrude","SWEPT_EDGE",EDGE,{"disambiguationData":[OSD([sQuery(id+"F10.wireOp",EDGE,"E58"),sQuery(id+"F10.wireOp",EDGE,"E66")])]});
            var Q7;
            Q7=makeQuery(id+"F11.opExtrude","SWEPT_EDGE",EDGE,{"disambiguationData":[OSD([sQuery(id+"F10.wireOp",EDGE,"E67"),sQuery(id+"F10.wireOp",EDGE,"E71.trimOffspring")])]});
            fillet(context, id + "F17", {"entities" : qUnion([Q0, Q1, Q2, Q3, Q4, Q5, Q6, Q7]), "radius" : 4 * mm, "allowEdgeOverflow" : false});
        }
        {
            var Q0;
            Q0=makeQuery(id+"F13.opExtrude","CAP_EDGE",EDGE,{"disambiguationData":[OSD([sQuery(id+"F12.wireOp",EDGE,"E74")])],"isStart":false});
            var Q1;
            Q1=makeQuery(id+"F13.opExtrude","CAP_EDGE",EDGE,{"disambiguationData":[OSD([sQuery(id+"F12.wireOp",EDGE,"E75")])],"isStart":false});
            var Q2;
            Q2=makeQuery(id+"F13.opExtrude","CAP_EDGE",EDGE,{"disambiguationData":[OSD([sQuery(id+"F12.wireOp",EDGE,"E79.MirrorCS")])],"isStart":false});
            var Q3;
            Q3=makeQuery(id+"F13.opExtrude","CAP_EDGE",EDGE,{"disambiguationData":[OSD([sQuery(id+"F12.wireOp",EDGE,"E77.MirrorCS")])],"isStart":false});
            fillet(context, id + "F18", {"entities" : qUnion([Q0, Q1, Q2, Q3]), "radius" : 3 * mm, "allowEdgeOverflow" : false});
        }
        {
            var Q0;
            Q0=makeQuery(id+"F13.boolean.opBoolean","INTERSECT",EDGE,{"derivedFrom":[makeQuery(id+"F11.opExtrude","CAP_FACE",FACE,{"disambiguationData":[OSD([sQuery(id+"F10.wireOp",EDGE,"E47.0"),sQuery(id+"F10.wireOp",EDGE,"E48.0"),sQuery(id+"F10.wireOp",EDGE,"E49.0"),sQuery(id+"F10.wireOp",EDGE,"E50.0"),sQuery(id+"F10.wireOp",EDGE,"E51.0"),sQuery(id+"F10.wireOp",EDGE,"E52.0"),sQuery(id+"F10.wireOp",EDGE,"E53.0"),sQuery(id+"F10.wireOp",EDGE,"E54.0"),sQuery(id+"F10.wireOp",EDGE,"E55"),sQuery(id+"F10.wireOp",EDGE,"E56"),sQuery(id+"F10.wireOp",EDGE,"E57"),sQuery(id+"F10.wireOp",EDGE,"E58"),sQuery(id+"F10.wireOp",EDGE,"E59.filletArc"),sQuery(id+"F10.wireOp",EDGE,"E60.filletArc"),sQuery(id+"F10.wireOp",EDGE,"E61.filletArc"),sQuery(id+"F10.wireOp",EDGE,"E62.filletArc"),sQuery(id+"F10.wireOp",EDGE,"E65"),sQuery(id+"F10.wireOp",EDGE,"E66"),sQuery(id+"F10.wireOp",EDGE,"E67"),sQuery(id+"F10.wireOp",EDGE,"E68.MirrorCS"),sQuery(id+"F10.wireOp",EDGE,"E69.MirrorCS"),sQuery(id+"F10.wireOp",EDGE,"E70.MirrorCS"),sQuery(id+"F10.wireOp",EDGE,"E71.trimOffspring"),sQuery(id+"F10.wireOp",EDGE,"E72.trimOffspring")])],"isStart":false}),makeQuery(id+"F13.opExtrude","SWEPT_FACE",FACE,{"disambiguationData":[OSD([sQuery(id+"F12.wireOp",EDGE,"E75")])]})]});
            var Q1;
            Q1=makeQuery(id+"F13.boolean.opBoolean","INTERSECT",EDGE,{"derivedFrom":[makeQuery(id+"F11.opExtrude","CAP_FACE",FACE,{"disambiguationData":[OSD([sQuery(id+"F10.wireOp",EDGE,"E47.0"),sQuery(id+"F10.wireOp",EDGE,"E48.0"),sQuery(id+"F10.wireOp",EDGE,"E49.0"),sQuery(id+"F10.wireOp",EDGE,"E50.0"),sQuery(id+"F10.wireOp",EDGE,"E51.0"),sQuery(id+"F10.wireOp",EDGE,"E52.0"),sQuery(id+"F10.wireOp",EDGE,"E53.0"),sQuery(id+"F10.wireOp",EDGE,"E54.0"),sQuery(id+"F10.wireOp",EDGE,"E55"),sQuery(id+"F10.wireOp",EDGE,"E56"),sQuery(id+"F10.wireOp",EDGE,"E57"),sQuery(id+"F10.wireOp",EDGE,"E58"),sQuery(id+"F10.wireOp",EDGE,"E59.filletArc"),sQuery(id+"F10.wireOp",EDGE,"E60.filletArc"),sQuery(id+"F10.wireOp",EDGE,"E61.filletArc"),sQuery(id+"F10.wireOp",EDGE,"E62.filletArc"),sQuery(id+"F10.wireOp",EDGE,"E65"),sQuery(id+"F10.wireOp",EDGE,"E66"),sQuery(id+"F10.wireOp",EDGE,"E67"),sQuery(id+"F10.wireOp",EDGE,"E68.MirrorCS"),sQuery(id+"F10.wireOp",EDGE,"E69.MirrorCS"),sQuery(id+"F10.wireOp",EDGE,"E70.MirrorCS"),sQuery(id+"F10.wireOp",EDGE,"E71.trimOffspring"),sQuery(id+"F10.wireOp",EDGE,"E72.trimOffspring")])],"isStart":false}),makeQuery(id+"F13.opExtrude","SWEPT_FACE",FACE,{"disambiguationData":[OSD([sQuery(id+"F12.wireOp",EDGE,"E79.MirrorCS")])]})]});
            var Q2;
            Q2=makeQuery(id+"F13.boolean.opBoolean","INTERSECT",EDGE,{"derivedFrom":[makeQuery(id+"F11.opExtrude","CAP_FACE",FACE,{"disambiguationData":[OSD([sQuery(id+"F10.wireOp",EDGE,"E47.0"),sQuery(id+"F10.wireOp",EDGE,"E48.0"),sQuery(id+"F10.wireOp",EDGE,"E49.0"),sQuery(id+"F10.wireOp",EDGE,"E50.0"),sQuery(id+"F10.wireOp",EDGE,"E51.0"),sQuery(id+"F10.wireOp",EDGE,"E52.0"),sQuery(id+"F10.wireOp",EDGE,"E53.0"),sQuery(id+"F10.wireOp",EDGE,"E54.0"),sQuery(id+"F10.wireOp",EDGE,"E55"),sQuery(id+"F10.wireOp",EDGE,"E56"),sQuery(id+"F10.wireOp",EDGE,"E57"),sQuery(id+"F10.wireOp",EDGE,"E58"),sQuery(id+"F10.wireOp",EDGE,"E59.filletArc"),sQuery(id+"F10.wireOp",EDGE,"E60.filletArc"),sQuery(id+"F10.wireOp",EDGE,"E61.filletArc"),sQuery(id+"F10.wireOp",EDGE,"E62.filletArc"),sQuery(id+"F10.wireOp",EDGE,"E65"),sQuery(id+"F10.wireOp",EDGE,"E66"),sQuery(id+"F10.wireOp",EDGE,"E67"),sQuery(id+"F10.wireOp",EDGE,"E68.MirrorCS"),sQuery(id+"F10.wireOp",EDGE,"E69.MirrorCS"),sQuery(id+"F10.wireOp",EDGE,"E70.MirrorCS"),sQuery(id+"F10.wireOp",EDGE,"E71.trimOffspring"),sQuery(id+"F10.wireOp",EDGE,"E72.trimOffspring")])],"isStart":false}),makeQuery(id+"F13.opExtrude","SWEPT_FACE",FACE,{"disambiguationData":[OSD([sQuery(id+"F12.wireOp",EDGE,"E77.MirrorCS")])]})]});
            var Q3;
            Q3=makeQuery(id+"F13.boolean.opBoolean","INTERSECT",EDGE,{"derivedFrom":[makeQuery(id+"F11.opExtrude","CAP_FACE",FACE,{"disambiguationData":[OSD([sQuery(id+"F10.wireOp",EDGE,"E47.0"),sQuery(id+"F10.wireOp",EDGE,"E48.0"),sQuery(id+"F10.wireOp",EDGE,"E49.0"),sQuery(id+"F10.wireOp",EDGE,"E50.0"),sQuery(id+"F10.wireOp",EDGE,"E51.0"),sQuery(id+"F10.wireOp",EDGE,"E52.0"),sQuery(id+"F10.wireOp",EDGE,"E53.0"),sQuery(id+"F10.wireOp",EDGE,"E54.0"),sQuery(id+"F10.wireOp",EDGE,"E55"),sQuery(id+"F10.wireOp",EDGE,"E56"),sQuery(id+"F10.wireOp",EDGE,"E57"),sQuery(id+"F10.wireOp",EDGE,"E58"),sQuery(id+"F10.wireOp",EDGE,"E59.filletArc"),sQuery(id+"F10.wireOp",EDGE,"E60.filletArc"),sQuery(id+"F10.wireOp",EDGE,"E61.filletArc"),sQuery(id+"F10.wireOp",EDGE,"E62.filletArc"),sQuery(id+"F10.wireOp",EDGE,"E65"),sQuery(id+"F10.wireOp",EDGE,"E66"),sQuery(id+"F10.wireOp",EDGE,"E67"),sQuery(id+"F10.wireOp",EDGE,"E68.MirrorCS"),sQuery(id+"F10.wireOp",EDGE,"E69.MirrorCS"),sQuery(id+"F10.wireOp",EDGE,"E70.MirrorCS"),sQuery(id+"F10.wireOp",EDGE,"E71.trimOffspring"),sQuery(id+"F10.wireOp",EDGE,"E72.trimOffspring")])],"isStart":false}),makeQuery(id+"F13.opExtrude","SWEPT_FACE",FACE,{"disambiguationData":[OSD([sQuery(id+"F12.wireOp",EDGE,"E74")])]})]});
            fillet(context, id + "F19", {"entities" : qUnion([Q0, Q1, Q2, Q3]), "radius" : 4 * mm, "allowEdgeOverflow" : false});
        }
    });
